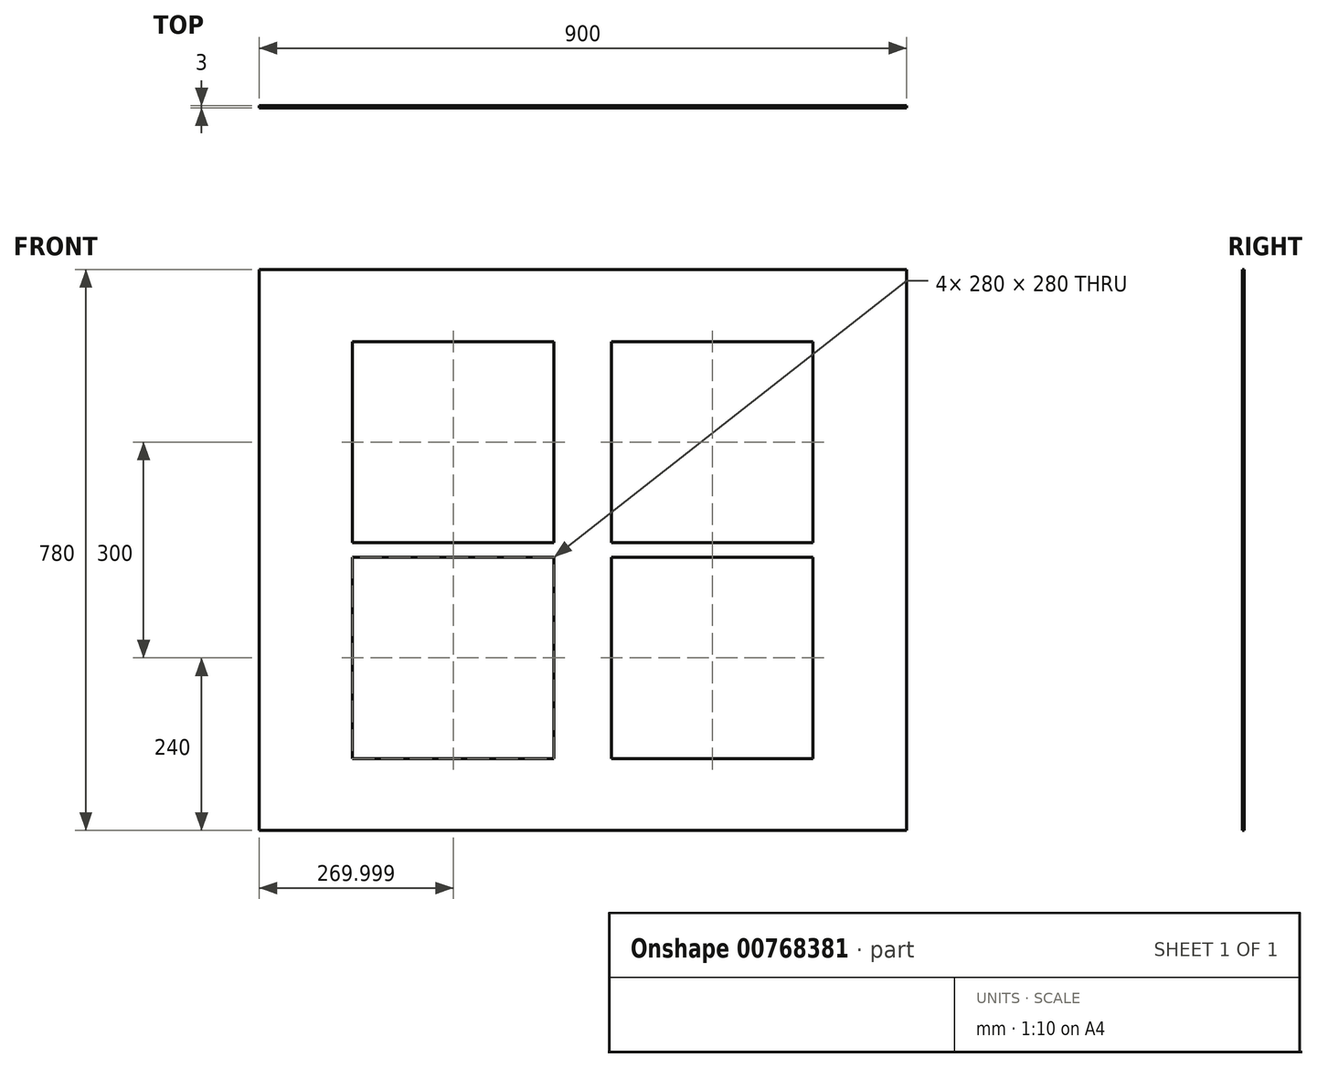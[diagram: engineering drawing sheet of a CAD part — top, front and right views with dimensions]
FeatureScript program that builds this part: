
annotation { "Feature Type Name" : "Feature", "Feature Type Description" : "" }
export const myFeature = defineFeature(function(context is Context, id is Id, definition is map)
    precondition{}
    {
        {
            var Q0;
            Q0=qCreatedBy(makeId("Front.planeOp"),FACE);
            var sketch = newSketch(context, id + "F0", { "sketchPlane" : qUnion([Q0])});
            skLineSegment(sketch, "E0.bottom", {"start": v(-660.08, 780) * mm, "end": v(239.92, 780) * mm});
            skLineSegment(sketch, "E0.top", {"start": v(-660.08, 0) * mm, "end": v(239.92, 0) * mm});
            skLineSegment(sketch, "E0.left", {"start": v(-660.08, 780) * mm, "end": v(-660.08, 0) * mm});
            skLineSegment(sketch, "E0.right", {"start": v(239.92, 780) * mm, "end": v(239.92, 0) * mm});
            skSolve(sketch);
        }
        {
            var Q0;
            Q0=makeQuery(id+"F0.imprint","IMPRINT",FACE,{"disambiguationData":[TD([[makeQuery(id+"F0.imprint","IMPRINT",EDGE,{"derivedFrom":sQuery(id+"F0.wireOp",EDGE,"E0.bottom")}),-1.0]])]});
            extrude(context, id + "F1", {"entities" : qUnion([Q0]), "depth" : 3 * mm, "offsetDistance" : 25 * mm});
        }
        {
            var Q0;
            Q0=makeQuery(id+"F1.opExtrude","CAP_FACE",FACE,{"disambiguationData":[OSD([sQuery(id+"F0.wireOp",EDGE,"E0.bottom"),sQuery(id+"F0.wireOp",EDGE,"E0.top"),sQuery(id+"F0.wireOp",EDGE,"E0.left"),sQuery(id+"F0.wireOp",EDGE,"E0.right")])],"isStart":false});
            var sketch = newSketch(context, id + "F2", { "sketchPlane" : qUnion([Q0])});
            skLineSegment(sketch, "E1", {"start": v(-210.08, 780) * mm, "end": v(-210.08, 0) * mm, "construction": true});
            skLineSegment(sketch, "E2", {"start": v(-660.08, 390) * mm, "end": v(239.92, 390) * mm, "construction": true});
            skLineSegment(sketch, "E3.bottom", {"start": v(-530.08, 680) * mm, "end": v(-250.08, 680) * mm});
            skLineSegment(sketch, "E3.top", {"start": v(-530.08, 400) * mm, "end": v(-250.08, 400) * mm});
            skLineSegment(sketch, "E3.left", {"start": v(-530.08, 680) * mm, "end": v(-530.08, 400) * mm});
            skLineSegment(sketch, "E3.right", {"start": v(-250.08, 680) * mm, "end": v(-250.08, 400) * mm});
            skLineSegment(sketch, "E4.MirrorCS", {"start": v(-250.08, 100) * mm, "end": v(-250.08, 380) * mm});
            skLineSegment(sketch, "E5.MirrorCS", {"start": v(-530.08, 100) * mm, "end": v(-250.08, 100) * mm});
            skLineSegment(sketch, "E6.MirrorCS", {"start": v(-530.08, 100) * mm, "end": v(-530.08, 380) * mm});
            skLineSegment(sketch, "E7.MirrorCS", {"start": v(-530.08, 380) * mm, "end": v(-250.08, 380) * mm});
            skLineSegment(sketch, "E8.MirrorCS", {"start": v(-170.08, 680) * mm, "end": v(-170.08, 400) * mm});
            skLineSegment(sketch, "E9.MirrorCS", {"start": v(109.92, 680) * mm, "end": v(-170.08, 680) * mm});
            skLineSegment(sketch, "E10.MirrorCS", {"start": v(109.92, 680) * mm, "end": v(109.92, 400) * mm});
            skLineSegment(sketch, "E11.MirrorCS", {"start": v(109.92, 400) * mm, "end": v(-170.08, 400) * mm});
            skLineSegment(sketch, "E12.MirrorCS", {"start": v(-170.08, 100) * mm, "end": v(-170.08, 380) * mm});
            skLineSegment(sketch, "E13.MirrorCS", {"start": v(109.92, 380) * mm, "end": v(-170.08, 380) * mm});
            skLineSegment(sketch, "E14.MirrorCS", {"start": v(109.92, 100) * mm, "end": v(109.92, 380) * mm});
            skLineSegment(sketch, "E15.MirrorCS", {"start": v(109.92, 100) * mm, "end": v(-170.08, 100) * mm});
            skSolve(sketch);
        }
        {
            var Q0;
            Q0=makeQuery(id+"F2.imprint","IMPRINT",FACE,{"disambiguationData":[TD([[makeQuery(id+"F2.imprint","IMPRINT",EDGE,{"derivedFrom":sQuery(id+"F2.wireOp",EDGE,"E3.bottom")}),-1.0]])]});
            var Q1;
            Q1=makeQuery(id+"F2.imprint","IMPRINT",FACE,{"disambiguationData":[TD([[makeQuery(id+"F2.imprint","IMPRINT",EDGE,{"derivedFrom":sQuery(id+"F2.wireOp",EDGE,"E8.MirrorCS")}),1.0]])]});
            var Q2;
            Q2=makeQuery(id+"F2.imprint","IMPRINT",FACE,{"disambiguationData":[TD([[makeQuery(id+"F2.imprint","IMPRINT",EDGE,{"derivedFrom":sQuery(id+"F2.wireOp",EDGE,"E12.MirrorCS")}),-1.0]])]});
            var Q3;
            Q3=makeQuery(id+"F2.imprint","IMPRINT",FACE,{"disambiguationData":[TD([[makeQuery(id+"F2.imprint","IMPRINT",EDGE,{"derivedFrom":sQuery(id+"F2.wireOp",EDGE,"E4.MirrorCS")}),1.0]])]});
            extrude(context, id + "F3", {"entities" : qUnion([Q0, Q1, Q2, Q3]), "operationType" : NewBodyOperationType.REMOVE, "oppositeDirection" : true, "depth" : 5 * mm, "offsetDistance" : 25 * mm});
        }
    });
